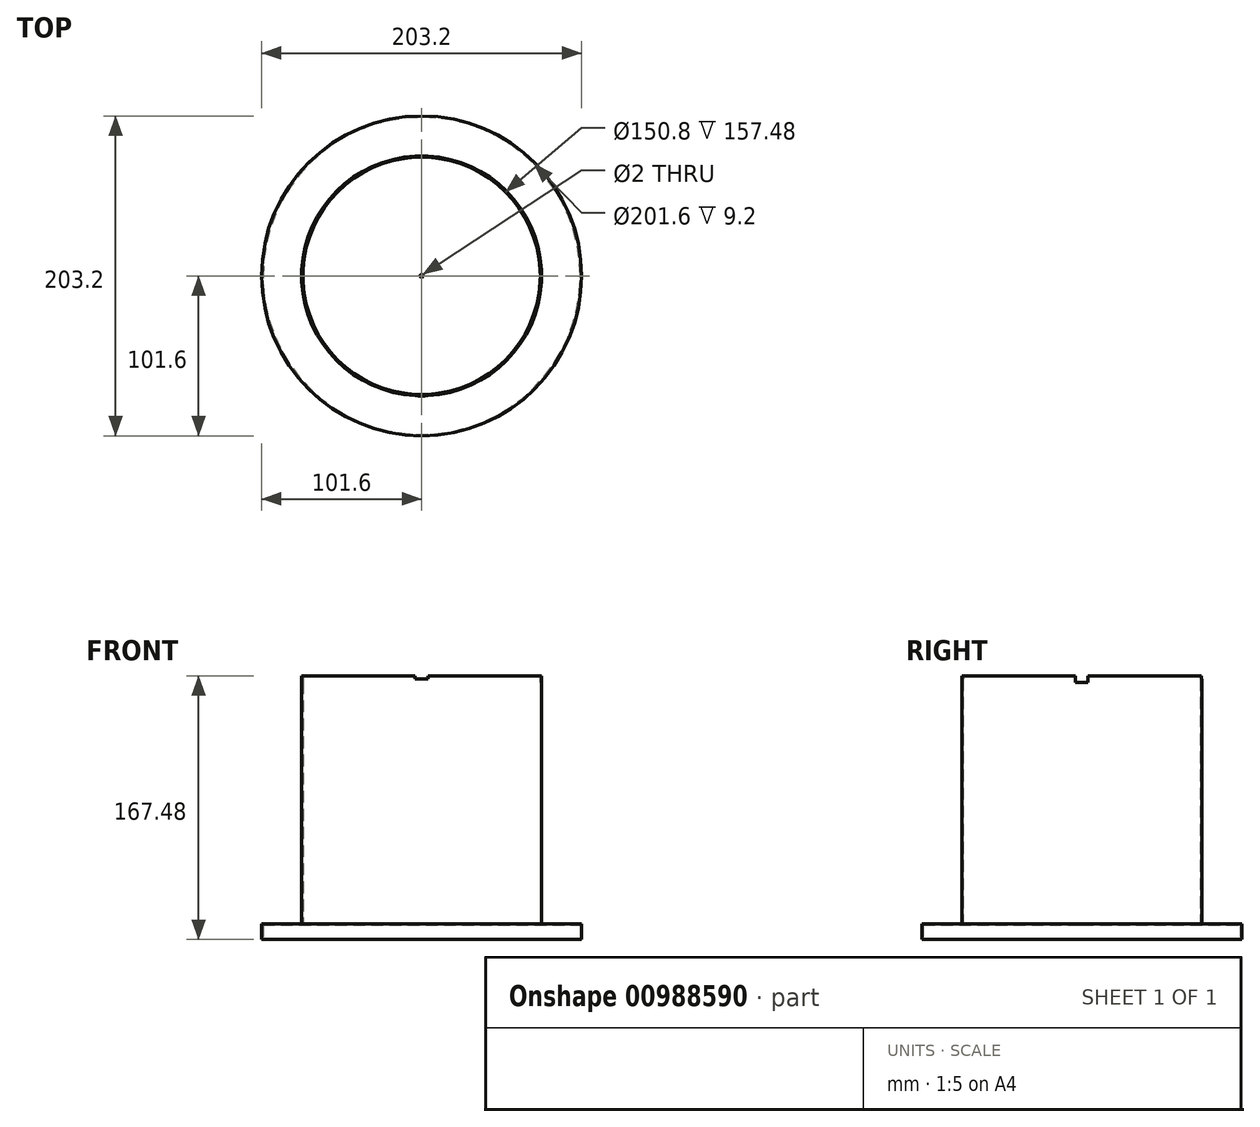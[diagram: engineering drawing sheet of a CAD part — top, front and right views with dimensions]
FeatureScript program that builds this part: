
annotation { "Feature Type Name" : "Feature", "Feature Type Description" : "" }
export const myFeature = defineFeature(function(context is Context, id is Id, definition is map)
    precondition{}
    {
        {
            var Q0;
            Q0=qCreatedBy(makeId("Top.planeOp"),FACE);
            var sketch = newSketch(context, id + "F0", { "sketchPlane" : qUnion([Q0])});
            skCircle(sketch, "E0", {"center": v(0, 0) * mm, "radius": 76.2 * mm});
            skSolve(sketch);
        }
        {
            var Q0;
            Q0=makeQuery(id+"F0.imprint","IMPRINT",FACE,{"disambiguationData":[TD([[makeQuery(id+"F0.imprint","IMPRINT",EDGE,{"derivedFrom":sQuery(id+"F0.wireOp",EDGE,"E0")}),1.0]])]});
            extrude(context, id + "F1", {"entities" : qUnion([Q0]), "depth" : 157.48 * mm + 0.8 * mm, "offsetDistance" : 25.4 * mm});
        }
        {
            var Q0;
            Q0=makeQuery(id+"F1.opExtrude","CAP_FACE",FACE,{"disambiguationData":[OSD([sQuery(id+"F0.wireOp",EDGE,"E0")])],"isStart":false});
            shell(context, id + "F2", {"entities" : qUnion([Q0]), "thickness" : 0.8 * mm});
        }
        {
            var Q0;
            {var subQ0=sQuery(id+"F0.wireOp",EDGE,"E0");Q0=makeQuery(id+"F2.opShell","OFFSET_FACE",FACE,{"disambiguationData":[OSD([subQ0]),TDD([makeQuery(id+"F1.opExtrude","CAP_FACE",FACE,{"disambiguationData":[OSD([subQ0])],"isStart":true})])]});}
            var sketch = newSketch(context, id + "F3", { "sketchPlane" : qUnion([Q0])});
            skCircle(sketch, "E1", {"center": v(0, 0) * mm, "radius": 1 * mm});
            skSolve(sketch);
        }
        {
            var Q0;
            Q0=qSketchRegion(id+"F3",true);
            extrude(context, id + "F4", {"entities" : qUnion([Q0]), "operationType" : NewBodyOperationType.REMOVE, "endBound" : BoundingType.UP_TO_NEXT, "oppositeDirection" : true, "depth" : 25.4 * mm, "offsetDistance" : 25.4 * mm});
        }
        {
            var Q0;
            Q0=qCreatedBy(makeId("Front.planeOp"),FACE);
            var sketch = newSketch(context, id + "F5", { "sketchPlane" : qUnion([Q0])});
            skLineSegment(sketch, "E2", {"start": v(-4, 158.28) * mm, "end": v(4, 158.28) * mm});
            skLineSegment(sketch, "E3", {"start": v(-4, 158.28) * mm, "end": v(-4, 156.28) * mm});
            skLineSegment(sketch, "E4", {"start": v(4, 158.28) * mm, "end": v(4, 156.28) * mm});
            skLineSegment(sketch, "E5", {"start": v(4, 156.28) * mm, "end": v(-4, 156.28) * mm});
            skLineSegment(sketch, "E6", {"start": v(0, 156.28) * mm, "end": v(0, 158.28) * mm, "construction": true});
            skSolve(sketch);
        }
        {
            var Q0;
            Q0=qSketchRegion(id+"F5",true);
            extrude(context, id + "F6", {"entities" : qUnion([Q0]), "operationType" : NewBodyOperationType.REMOVE, "endBound" : BoundingType.THROUGH_ALL, "oppositeDirection" : true, "depth" : 25.4 * mm, "offsetDistance" : 25.4 * mm, "hasSecondDirection" : true, "secondDirectionBound" : SecondDirectionBoundingType.THROUGH_ALL, "secondDirectionOppositeDirection" : false, "secondDirectionDepth" : 25.4 * mm});
        }
        {
            var Q0;
            Q0=qCreatedBy(makeId("Right.planeOp"),FACE);
            var sketch = newSketch(context, id + "F7", { "sketchPlane" : qUnion([Q0])});
            skLineSegment(sketch, "E7", {"start": v(-4, 158.28) * mm, "end": v(4, 158.28) * mm});
            skLineSegment(sketch, "E8", {"start": v(-4, 158.28) * mm, "end": v(-4, 154.28) * mm});
            skLineSegment(sketch, "E9", {"start": v(4, 158.28) * mm, "end": v(4, 154.28) * mm});
            skLineSegment(sketch, "E10", {"start": v(4, 154.28) * mm, "end": v(-4, 154.28) * mm});
            skSolve(sketch);
        }
        {
            var Q0;
            Q0=qSketchRegion(id+"F7",true);
            extrude(context, id + "F8", {"entities" : qUnion([Q0]), "operationType" : NewBodyOperationType.REMOVE, "endBound" : BoundingType.THROUGH_ALL, "oppositeDirection" : true, "depth" : 25.4 * mm, "offsetDistance" : 25.4 * mm, "hasSecondDirection" : true, "secondDirectionBound" : SecondDirectionBoundingType.THROUGH_ALL, "secondDirectionOppositeDirection" : false, "secondDirectionDepth" : 25.4 * mm});
        }
        {
            var Q0;
            Q0=qCreatedBy(makeId("Front.planeOp"),FACE);
            var sketch = newSketch(context, id + "F9", { "sketchPlane" : qUnion([Q0])});
            skLineSegment(sketch, "E11", {"start": v(76.2, 0) * mm, "end": v(100.8, 0) * mm});
            skLineSegment(sketch, "E12", {"start": v(100.8, 0) * mm, "end": v(100.8, -9.2) * mm});
            skLineSegment(sketch, "E13.0", {"start": v(101.6, 0.8) * mm, "end": v(101.6, -9.2) * mm});
            skLineSegment(sketch, "E13.1", {"start": v(76.2, 0.8) * mm, "end": v(101.6, 0.8) * mm});
            skLineSegment(sketch, "E14", {"start": v(101.6, -9.2) * mm, "end": v(100.8, -9.2) * mm});
            skLineSegment(sketch, "E15", {"start": v(76.2, 0.8) * mm, "end": v(76.2, 0) * mm});
            skLineSegment(sketch, "E16", {"start": v(0, 0) * mm, "end": v(0, 37.14) * mm, "construction": true});
            skSolve(sketch);
        }
        {
            var Q0;
            Q0=makeQuery(id+"F9.imprint","IMPRINT",FACE,{"disambiguationData":[TD([[makeQuery(id+"F9.imprint","IMPRINT",EDGE,{"derivedFrom":sQuery(id+"F9.wireOp",EDGE,"E11")}),1.0]])]});
            var Q1;
            Q1=sQuery(id+"F9.wireOp",EDGE,"E16");
            revolve(context, id + "F10", {"operationType" : NewBodyOperationType.ADD, "surfaceOperationType" : NewSurfaceOperationType.NEW, "entities" : qUnion([Q0]), "axis" : qUnion([Q1]), "revolveType" : RevolveType.FULL});
        }
    });
